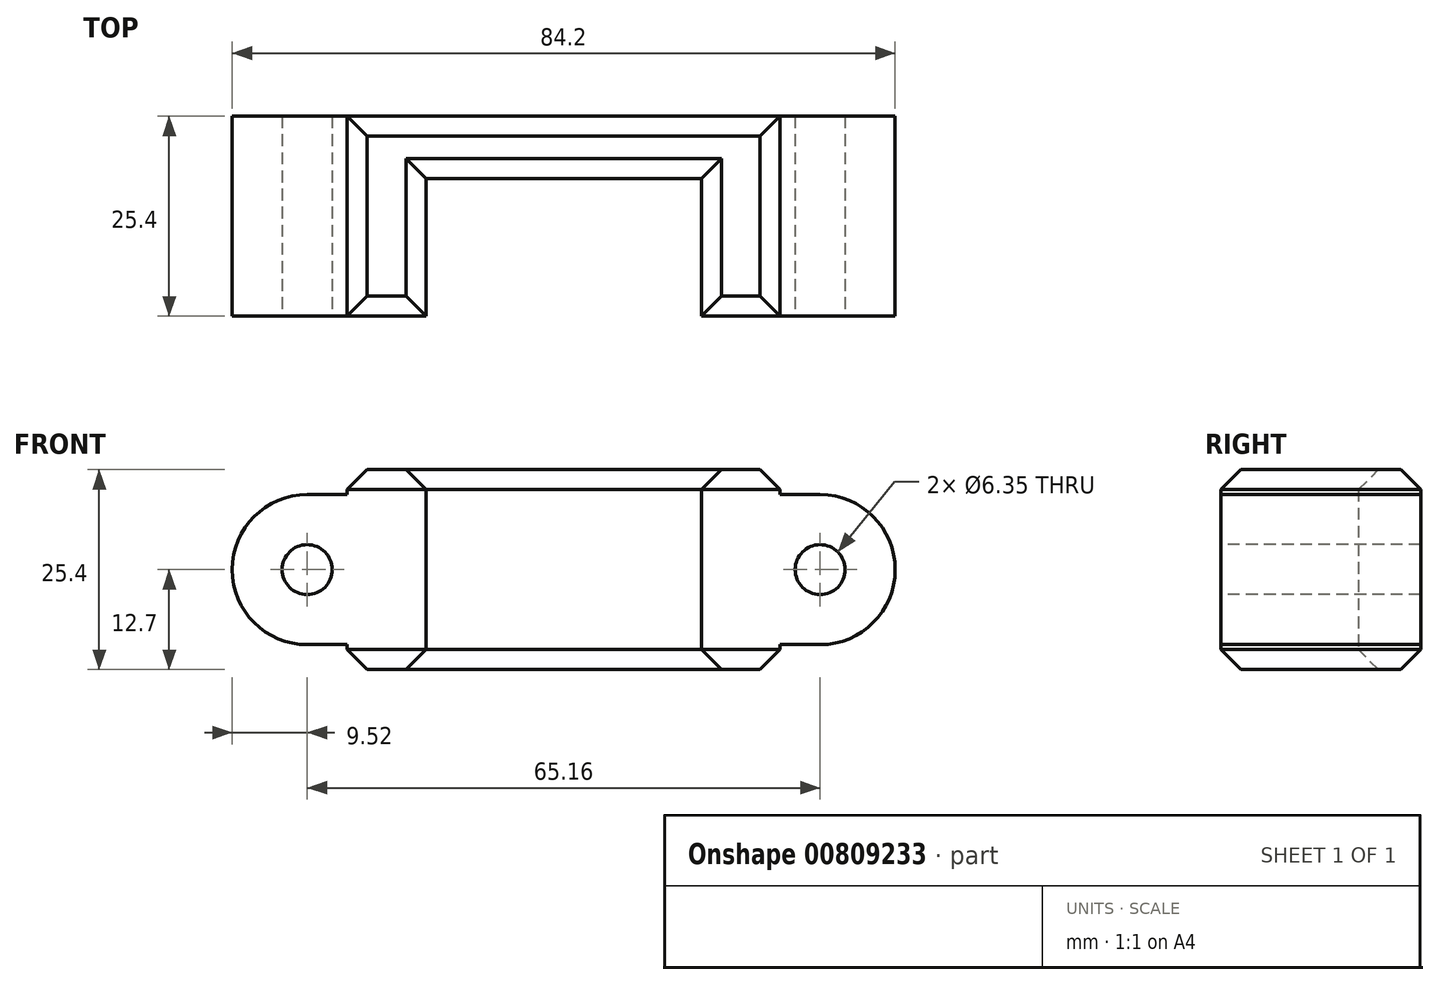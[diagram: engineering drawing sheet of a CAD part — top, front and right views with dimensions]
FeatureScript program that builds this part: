
annotation { "Feature Type Name" : "Feature", "Feature Type Description" : "" }
export const myFeature = defineFeature(function(context is Context, id is Id, definition is map)
    precondition{}
    {
        {
            var Q0;
            Q0=qCreatedBy(makeId("Top.planeOp"),FACE);
            var sketch = newSketch(context, id + "F0", { "sketchPlane" : qUnion([Q0])});
            skLineSegment(sketch, "E0.top", {"start": v(17.5, 17.5) * mm, "end": v(-17.5, 17.5) * mm});
            skLineSegment(sketch, "E0.left", {"start": v(17.5, 0) * mm, "end": v(17.5, 17.5) * mm});
            skLineSegment(sketch, "E0.right", {"start": v(-17.5, 0) * mm, "end": v(-17.5, 17.5) * mm});
            skPoint(sketch, "E0.middle", {"position": v(0, 0) * mm});
            skLineSegment(sketch, "E1.top", {"start": v(27.5, 25.4) * mm, "end": v(-27.5, 25.4) * mm});
            skLineSegment(sketch, "E1.left", {"start": v(27.5, 0) * mm, "end": v(27.5, 25.4) * mm});
            skLineSegment(sketch, "E1.right", {"start": v(-27.5, 0) * mm, "end": v(-27.5, 25.4) * mm});
            skLineSegment(sketch, "E2", {"start": v(-27.5, 0) * mm, "end": v(27.5, 0) * mm});
            skPoint(sketch, "E3.orphan", {"position": v(27.5, -25.4) * mm});
            skPoint(sketch, "E4.orphan", {"position": v(-27.5, -25.4) * mm});
            skPoint(sketch, "E5.orphan", {"position": v(17.5, -17.5) * mm});
            skPoint(sketch, "E6.orphan", {"position": v(-17.5, -17.5) * mm});
            skSolve(sketch);
        }
        {
            var Q0;
            Q0=makeQuery(id+"F0.imprint","IMPRINT",FACE,{"disambiguationData":[TD([[makeQuery(id+"F0.imprint","IMPRINT",EDGE,{"derivedFrom":sQuery(id+"F0.wireOp",EDGE,"E0.top")}),-1.0]])]});
            extrude(context, id + "F1", {"entities" : qUnion([Q0]), "depth" : 25.4 * mm, "offsetDistance" : 25.4 * mm});
        }
        {
            var Q0;
            Q0=qCreatedBy(makeId("Front.planeOp"),FACE);
            var sketch = newSketch(context, id + "F2", { "sketchPlane" : qUnion([Q0])});
            skCircle(sketch, "E7", {"center": v(-32.58, 12.7) * mm, "radius": 3.18 * mm});
            skLineSegment(sketch, "E8", {"start": v(-27.5, 22.23) * mm, "end": v(-32.58, 22.23) * mm});
            skLineSegment(sketch, "E9", {"start": v(-27.5, 3.18) * mm, "end": v(-32.58, 3.18) * mm});
            skArc(sketch, "E10", {"start": v(-32.58, 22.23) * mm, "mid": v(-42.1, 12.7) * mm, "end": v(-32.58, 3.18) * mm});
            skLineSegment(sketch, "E11", {"start": v(-27.5, 22.23) * mm, "end": v(-27.5, 3.18) * mm});
            skSolve(sketch);
        }
        {
            var Q0;
            Q0=makeQuery(id+"F2.imprint","IMPRINT",FACE,{"disambiguationData":[TD([[makeQuery(id+"F2.imprint","IMPRINT",EDGE,{"derivedFrom":sQuery(id+"F2.wireOp",EDGE,"E7")}),-1.0]])]});
            extrude(context, id + "F3", {"entities" : qUnion([Q0]), "oppositeDirection" : true, "depth" : 25.4 * mm, "offsetDistance" : 25.4 * mm});
        }
        {
            var Q0;
            Q0=makeQuery(id+"F1.opExtrude","CAP_FACE",FACE,{"disambiguationData":[OSD([sQuery(id+"F0.wireOp",EDGE,"E0.top"),sQuery(id+"F0.wireOp",EDGE,"E0.left"),sQuery(id+"F0.wireOp",EDGE,"E0.right"),sQuery(id+"F0.wireOp",EDGE,"E1.top"),sQuery(id+"F0.wireOp",EDGE,"E1.left"),sQuery(id+"F0.wireOp",EDGE,"E1.right"),sQuery(id+"F0.wireOp",EDGE,"E2")])],"isStart":true});
            var Q1;
            Q1=makeQuery(id+"F1.opExtrude","CAP_FACE",FACE,{"disambiguationData":[OSD([sQuery(id+"F0.wireOp",EDGE,"E0.top"),sQuery(id+"F0.wireOp",EDGE,"E0.left"),sQuery(id+"F0.wireOp",EDGE,"E0.right"),sQuery(id+"F0.wireOp",EDGE,"E1.top"),sQuery(id+"F0.wireOp",EDGE,"E1.left"),sQuery(id+"F0.wireOp",EDGE,"E1.right"),sQuery(id+"F0.wireOp",EDGE,"E2")])],"isStart":false});
            chamfer(context, id + "F4", {"entities" : qUnion([Q0, Q1]), "width" : 2.54 * mm, "tangentPropagation" : true});
        }
        {
            var Q0;
            Q0=makeQuery(id+"F3.opExtrude","SWEPT_BODY",BODY,{"disambiguationData":[OSD([sQuery(id+"F2.wireOp",EDGE,"E7"),sQuery(id+"F2.wireOp",EDGE,"E8"),sQuery(id+"F2.wireOp",EDGE,"E9"),sQuery(id+"F2.wireOp",EDGE,"E10"),sQuery(id+"F2.wireOp",EDGE,"E11")])]});
            var Q1;
            Q1=qCreatedBy(makeId("Right.planeOp"),FACE);
            mirror(context, id + "F5", {"operationType" : NewBodyOperationType.ADD, "entities" : qUnion([Q0]), "mirrorPlane" : qUnion([Q1])});
        }
    });
